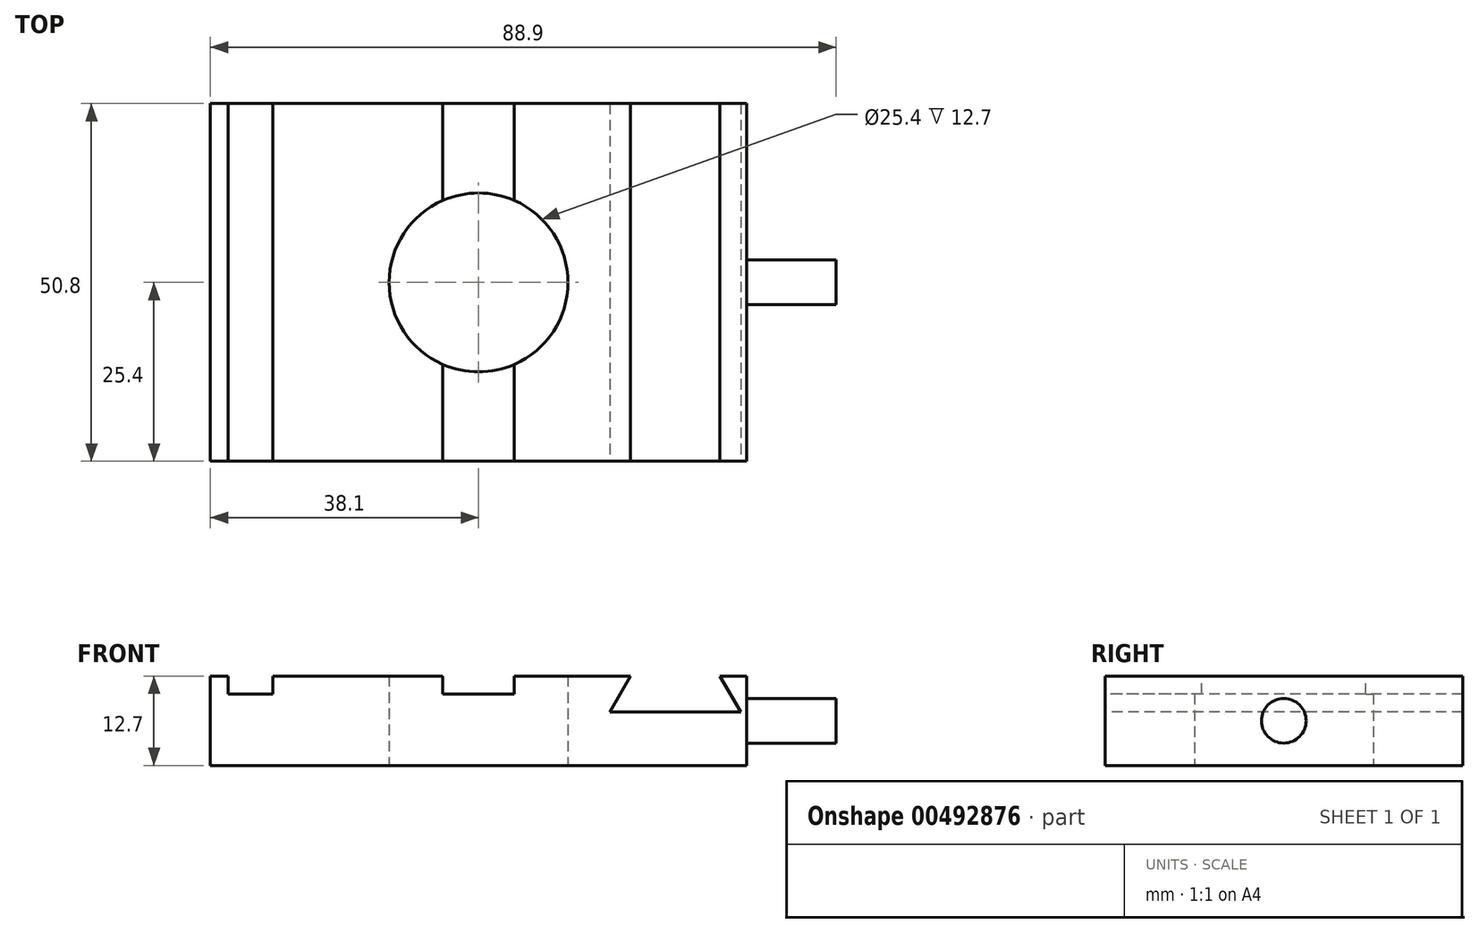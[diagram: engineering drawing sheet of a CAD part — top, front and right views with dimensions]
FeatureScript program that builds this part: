
annotation { "Feature Type Name" : "Feature", "Feature Type Description" : "" }
export const myFeature = defineFeature(function(context is Context, id is Id, definition is map)
    precondition{}
    {
        {
            var Q0;
            Q0=qCreatedBy(makeId("Top.planeOp"),FACE);
            var sketch = newSketch(context, id + "F0", { "sketchPlane" : qUnion([Q0])});
            skLineSegment(sketch, "E0.bottom", {"start": v(-38.1, 25.4) * mm, "end": v(38.1, 25.4) * mm});
            skLineSegment(sketch, "E0.top", {"start": v(-38.1, -25.4) * mm, "end": v(38.1, -25.4) * mm});
            skLineSegment(sketch, "E0.left", {"start": v(-38.1, 25.4) * mm, "end": v(-38.1, -25.4) * mm});
            skLineSegment(sketch, "E0.right", {"start": v(38.1, 25.4) * mm, "end": v(38.1, -25.4) * mm});
            skPoint(sketch, "E0.middle", {"position": v(0, 0) * mm});
            skCircle(sketch, "E1", {"center": v(0, 0) * mm, "radius": 12.7 * mm});
            skSolve(sketch);
        }
        {
            var Q0;
            Q0=makeQuery(id+"F0.imprint","IMPRINT",FACE,{"disambiguationData":[TD([[makeQuery(id+"F0.imprint","IMPRINT",EDGE,{"derivedFrom":sQuery(id+"F0.wireOp",EDGE,"E0.bottom")}),-1.0]])]});
            extrude(context, id + "F1", {"entities" : qUnion([Q0]), "depth" : 12.7 * mm, "offsetDistance" : 25.4 * mm});
        }
        {
            var Q0;
            Q0=makeQuery(id+"F1.opExtrude","CAP_FACE",FACE,{"disambiguationData":[OSD([sQuery(id+"F0.wireOp",EDGE,"E0.bottom"),sQuery(id+"F0.wireOp",EDGE,"E0.top"),sQuery(id+"F0.wireOp",EDGE,"E0.left"),sQuery(id+"F0.wireOp",EDGE,"E0.right"),sQuery(id+"F0.wireOp",EDGE,"E1")])],"isStart":false});
            var sketch = newSketch(context, id + "F2", { "sketchPlane" : qUnion([Q0])});
            skLineSegment(sketch, "E2.bottom", {"start": v(-5.08, 25.4) * mm, "end": v(5.08, 25.4) * mm});
            skLineSegment(sketch, "E2.top", {"start": v(-5.08, -25.4) * mm, "end": v(5.08, -25.4) * mm});
            skLineSegment(sketch, "E2.left", {"start": v(-5.08, 25.4) * mm, "end": v(-5.08, -25.4) * mm});
            skLineSegment(sketch, "E2.right", {"start": v(5.08, 25.4) * mm, "end": v(5.08, -25.4) * mm});
            skPoint(sketch, "E3", {"position": v(0, 0) * mm});
            skLineSegment(sketch, "E4", {"start": v(0, 25.4) * mm, "end": v(0, -25.4) * mm, "construction": true});
            skLineSegment(sketch, "E5.bottom", {"start": v(-35.56, 25.4) * mm, "end": v(-29.21, 25.4) * mm});
            skLineSegment(sketch, "E5.top", {"start": v(-35.56, -25.4) * mm, "end": v(-29.21, -25.4) * mm});
            skLineSegment(sketch, "E5.left", {"start": v(-35.56, 25.4) * mm, "end": v(-35.56, -25.4) * mm});
            skLineSegment(sketch, "E5.right", {"start": v(-29.21, 25.4) * mm, "end": v(-29.21, -25.4) * mm});
            skSolve(sketch);
        }
        {
            var Q0;
            {var subQ0=sQuery(id+"F2.wireOp",EDGE,"E2.top");Q0=makeQuery(id+"F2.imprint","IMPRINT",FACE,{"disambiguationData":[TD([[makeQuery(id+"F2.imprint","IMPRINT",EDGE,{"derivedFrom":subQ0}),1.0]])]});}
            var Q1;
            {var subQ0=sQuery(id+"F2.wireOp",EDGE,"E2.bottom");Q1=makeQuery(id+"F2.imprint","IMPRINT",FACE,{"disambiguationData":[TD([[makeQuery(id+"F2.imprint","IMPRINT",EDGE,{"derivedFrom":subQ0}),-1.0]])]});}
            var Q2;
            Q2=makeQuery(id+"F2.imprint","IMPRINT",FACE,{"disambiguationData":[TD([[makeQuery(id+"F2.imprint","IMPRINT",EDGE,{"derivedFrom":sQuery(id+"F2.wireOp",EDGE,"E5.bottom")}),-1.0]])]});
            extrude(context, id + "F3", {"entities" : qUnion([Q0, Q1, Q2]), "operationType" : NewBodyOperationType.REMOVE, "oppositeDirection" : true, "depth" : 2.54 * mm, "offsetDistance" : 25.4 * mm});
        }
        {
            var Q0;
            Q0=makeQuery(id+"F1.opExtrude","SWEPT_FACE",FACE,{"disambiguationData":[OSD([sQuery(id+"F0.wireOp",EDGE,"E0.top")])]});
            var sketch = newSketch(context, id + "F4", { "sketchPlane" : qUnion([Q0])});
            skLineSegment(sketch, "E6", {"start": v(21.59, 12.7) * mm, "end": v(18.66, 7.62) * mm});
            skLineSegment(sketch, "E7", {"start": v(18.66, 7.62) * mm, "end": v(37.22, 7.62) * mm});
            skLineSegment(sketch, "E8", {"start": v(37.22, 7.62) * mm, "end": v(34.3, 12.7) * mm});
            skLineSegment(sketch, "E9", {"start": v(34.3, 12.7) * mm, "end": v(21.59, 12.7) * mm});
            skLineSegment(sketch, "E10", {"start": v(27.94, 7.62) * mm, "end": v(27.94, 12.7) * mm, "construction": true});
            skSolve(sketch);
        }
        {
            var Q0;
            Q0=makeQuery(id+"F4.imprint","IMPRINT",FACE,{"disambiguationData":[TD([[makeQuery(id+"F4.imprint","IMPRINT",EDGE,{"derivedFrom":sQuery(id+"F4.wireOp",EDGE,"E6")}),1.0]])]});
            extrude(context, id + "F5", {"entities" : qUnion([Q0]), "operationType" : NewBodyOperationType.REMOVE, "oppositeDirection" : true, "depth" : 50.85 * mm, "offsetDistance" : 25.4 * mm});
        }
        {
            var Q0;
            Q0=makeQuery(id+"F1.opExtrude","SWEPT_FACE",FACE,{"disambiguationData":[OSD([sQuery(id+"F0.wireOp",EDGE,"E0.right")])]});
            var sketch = newSketch(context, id + "F6", { "sketchPlane" : qUnion([Q0])});
            skCircle(sketch, "E11", {"center": v(0, 6.35) * mm, "radius": 3.18 * mm});
            skSolve(sketch);
        }
        {
            var Q0;
            Q0 = qSketchRegion(id + "F6", true);
            extrude(context, id + "F7", {"entities" : qUnion([Q0]), "operationType" : NewBodyOperationType.ADD, "depth" : 12.7 * mm, "offsetDistance" : 25.4 * mm});
        }
    });
